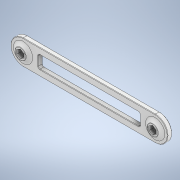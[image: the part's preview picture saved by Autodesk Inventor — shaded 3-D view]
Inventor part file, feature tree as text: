
AUTODESK INVENTOR PART (.ipt)
format: ipt  version: 2020 (Build 240168000, 168)  size: 256,000 bytes
history: native  units: mm
features: sketch x4, extrude x4, fillet x4, projected_geometry x4, hole x1
ambient origin geometry x8: Origin, YZ Plane, XZ Plane, XY Plane, X Axis, Y Axis, Z Axis, Center Point
bodies: Solid1 (feature_tree)
feature tree (17):
  sketch  "Sketch1"  dims[d2=149.0mm d3=28.0mm]
  extrude  "Extrusion1"  Depth=28.0mm
  extrude  "Extrusion2"  Depth=7.0mm
  hole  "Hole1"  [1 undecoded]
  extrude  "Extrusion3"  Depth=8.25mm
  extrude  "Extrusion4"  Depth=2.0mm
  fillet  "Fillet3"  Radius=12.5mm
  fillet  "Fillet1"  Radius=3.0mm
  fillet  "Fillet2"  Radius=5.0mm
  fillet  "Fillet4"  Radius=0.5mm
  sketch  "Sketch2"  dims[d4=5.0mm d5=0.0mm d6=7.0mm]
  projected_geometry  "Projected Loop1"
  sketch  "Sketch4"  dims[d8=0.0mm d9=0.0mm d10=2.0mm]
  projected_geometry  "Projected Loop2"
  sketch  "Sketch5"  dims[d11=14.0mm d12=5.4mm d13=6.0mm d14=4.0mm d15=2.0mm d16=90.0deg d17=8.0mm d18=90.0deg d19=8.25mm d20=12.5mm d21=12.5mm d22=3.0mm d23=0.0mm d24=5.0mm d25=0.5mm d26=3.0mm d27=2.0mm d28=0.0mm]
  projected_geometry  "Projected Loop3"
  projected_geometry  "Projected Loop4"
note: 1 required parameter value undecoded (feature->parameter linkage not recoverable at this tier; creation-order binding heuristic only, values carry confidence <= 0.55)
